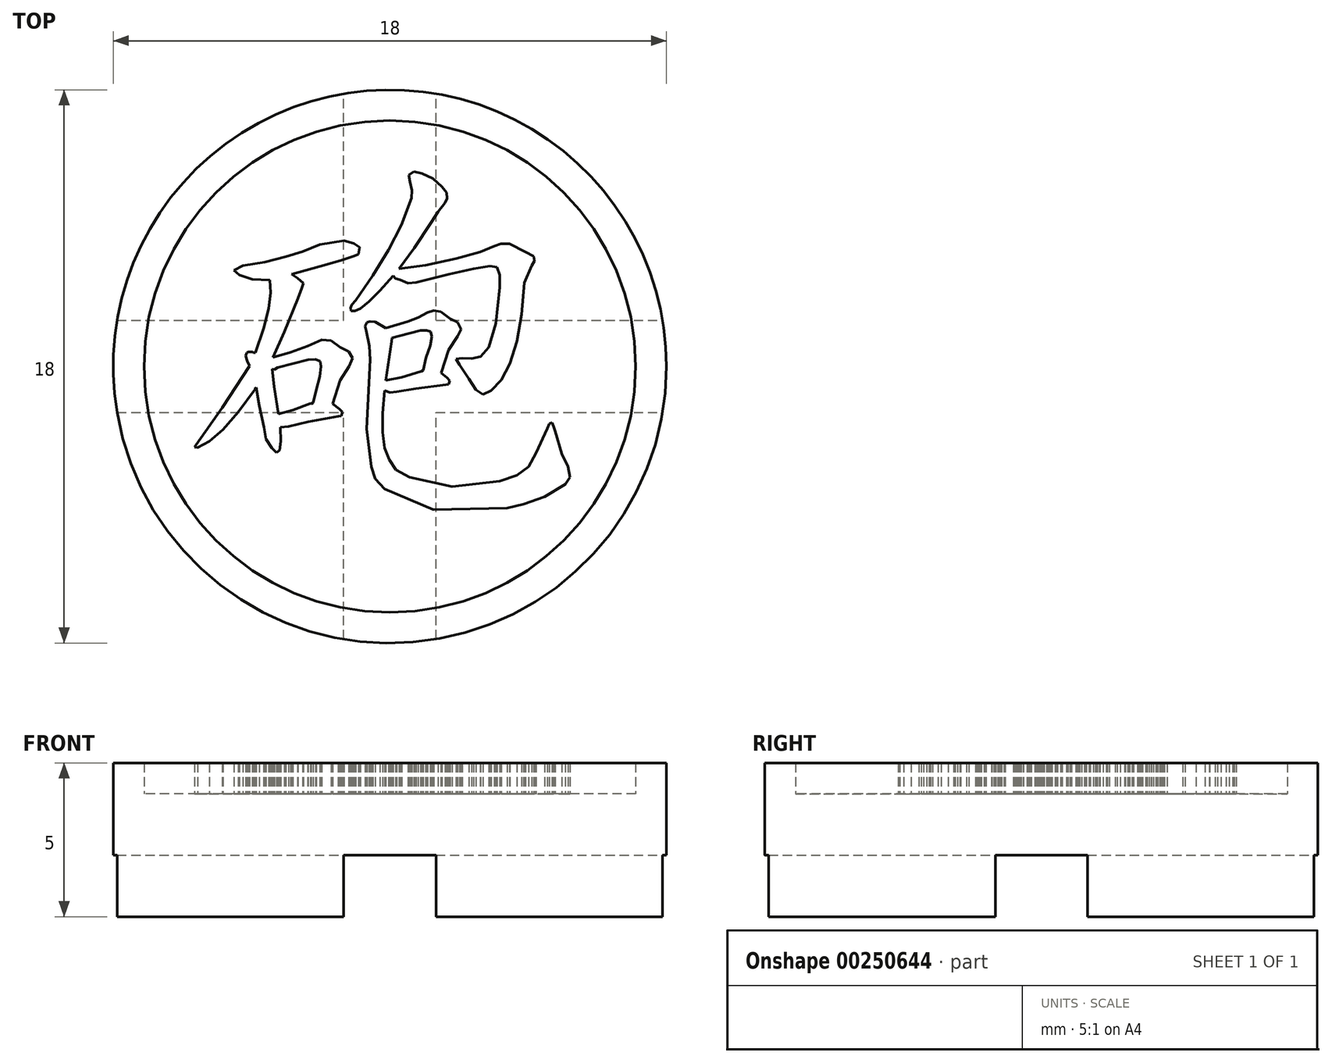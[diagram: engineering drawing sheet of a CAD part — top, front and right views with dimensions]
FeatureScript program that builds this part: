
annotation { "Feature Type Name" : "Feature", "Feature Type Description" : "" }
export const myFeature = defineFeature(function(context is Context, id is Id, definition is map)
    precondition{}
    {
        {
            var Q0;
            Q0=qCreatedBy(makeId("Top.planeOp"),FACE);
            var sketch = newSketch(context, id + "F0", { "sketchPlane" : qUnion([Q0])});
            skCircle(sketch, "E0", {"center": v(-31.33, 19.76) * mm, "radius": 9 * mm});
            skSolve(sketch);
        }
        {
            var Q0;
            Q0=qSketchRegion(id+"F0",true);
            extrude(context, id + "F1", {"entities" : qUnion([Q0]), "depth" : 4 * mm});
        }
        {
            var Q0;
            Q0=makeQuery(id+"F1.opExtrude","CAP_FACE",FACE,{"disambiguationData":[OSD([sQuery(id+"F0.wireOp",EDGE,"E0")])],"isStart":false});
            var sketch = newSketch(context, id + "F2", { "sketchPlane" : qUnion([Q0])});
            skCircle(sketch, "E1", {"center": v(-31.33, 19.76) * mm, "radius": 8 * mm});
            skCircle(sketch, "E2", {"center": v(-31.33, 19.76) * mm, "radius": 9 * mm});
            skSolve(sketch);
        }
        {
            var Q0;
            Q0=makeQuery(id+"F1.opExtrude","CAP_FACE",FACE,{"disambiguationData":[OSD([sQuery(id+"F0.wireOp",EDGE,"E0")])],"isStart":true});
            var sketch = newSketch(context, id + "F3", { "sketchPlane" : qUnion([Q0])});
            skLineSegment(sketch, "E3", {"start": v(-31.33, -19.76) * mm, "end": v(-22.33, -19.76) * mm, "construction": true});
            skLineSegment(sketch, "E4", {"start": v(-31.33, -19.76) * mm, "end": v(-31.33, -10.76) * mm, "construction": true});
            skLineSegment(sketch, "E5", {"start": v(-31.33, -19.76) * mm, "end": v(-40.33, -19.76) * mm, "construction": true});
            skLineSegment(sketch, "E6", {"start": v(-31.33, -19.76) * mm, "end": v(-31.33, -28.76) * mm, "construction": true});
            skLineSegment(sketch, "E7.bottom", {"start": v(-40.33, -28.76) * mm, "end": v(-22.33, -28.76) * mm});
            skLineSegment(sketch, "E7.top", {"start": v(-40.33, -10.76) * mm, "end": v(-22.33, -10.76) * mm});
            skLineSegment(sketch, "E7.left", {"start": v(-22.33, -10.76) * mm, "end": v(-22.33, -28.76) * mm});
            skLineSegment(sketch, "E7.right", {"start": v(-40.33, -10.76) * mm, "end": v(-40.33, -28.76) * mm});
            skPoint(sketch, "E8", {"position": v(-31.33, -28.76) * mm});
            skPoint(sketch, "E9", {"position": v(-40.33, -19.76) * mm});
            skPoint(sketch, "E10", {"position": v(-22.33, -19.76) * mm});
            skPoint(sketch, "E11", {"position": v(-31.33, -10.76) * mm});
            skLineSegment(sketch, "E12.bottom", {"start": v(-32.83, -10.76) * mm, "end": v(-29.83, -10.76) * mm});
            skLineSegment(sketch, "E12.top", {"start": v(-32.83, -28.76) * mm, "end": v(-29.83, -28.76) * mm});
            skLineSegment(sketch, "E12.left", {"start": v(-32.83, -10.76) * mm, "end": v(-32.83, -28.76) * mm});
            skLineSegment(sketch, "E12.right", {"start": v(-29.83, -10.76) * mm, "end": v(-29.83, -28.76) * mm});
            skLineSegment(sketch, "E13.bottom", {"start": v(-40.33, -18.26) * mm, "end": v(-22.33, -18.26) * mm});
            skLineSegment(sketch, "E13.top", {"start": v(-40.33, -21.26) * mm, "end": v(-22.33, -21.26) * mm});
            skLineSegment(sketch, "E13.left", {"start": v(-40.33, -18.26) * mm, "end": v(-40.33, -21.26) * mm});
            skLineSegment(sketch, "E13.right", {"start": v(-22.33, -18.26) * mm, "end": v(-22.33, -21.26) * mm});
            skSolve(sketch);
        }
        {
            var Q0;
            {var subQ1=sQuery(id+"F3.wireOp",EDGE,"E12.bottom");var subQ3=makeQuery(id+"F1.opExtrude","CAP_EDGE",EDGE,{"disambiguationData":[OSD([sQuery(id+"F0.wireOp",EDGE,"E0")])],"isStart":true});var subQ4=makeQuery(id+"F3.imprint","INTERSECT",VERTEX,{"derivedFrom":[subQ3,subQ1]});Q0=makeQuery(id+"F3.imprint","IMPRINT",FACE,{"disambiguationData":[TD([[makeQuery(id+"F3.imprint","IMPRINT",EDGE,{"disambiguationData":[TD([[subQ4,1.0]])],"derivedFrom":subQ3}),1.0]])]});}
            var Q1;
            {var subQ1=sQuery(id+"F3.wireOp",EDGE,"E12.bottom");var subQ3=makeQuery(id+"F1.opExtrude","CAP_EDGE",EDGE,{"disambiguationData":[OSD([sQuery(id+"F0.wireOp",EDGE,"E0")])],"isStart":true});var subQ4=makeQuery(id+"F3.imprint","INTERSECT",VERTEX,{"derivedFrom":[subQ3,subQ1]});Q1=makeQuery(id+"F3.imprint","IMPRINT",FACE,{"disambiguationData":[TD([[makeQuery(id+"F3.imprint","IMPRINT",EDGE,{"disambiguationData":[TD([[subQ4,-1.0]])],"derivedFrom":subQ3}),1.0]])]});}
            var Q2;
            {var subQ1=sQuery(id+"F3.wireOp",EDGE,"E12.top");var subQ3=makeQuery(id+"F1.opExtrude","CAP_EDGE",EDGE,{"disambiguationData":[OSD([sQuery(id+"F0.wireOp",EDGE,"E0")])],"isStart":true});var subQ4=makeQuery(id+"F3.imprint","INTERSECT",VERTEX,{"derivedFrom":[subQ3,subQ1]});Q2=makeQuery(id+"F3.imprint","IMPRINT",FACE,{"disambiguationData":[TD([[makeQuery(id+"F3.imprint","IMPRINT",EDGE,{"disambiguationData":[TD([[subQ4,-1.0]])],"derivedFrom":subQ3}),1.0]])]});}
            var Q3;
            {var subQ1=sQuery(id+"F3.wireOp",EDGE,"E12.top");var subQ3=makeQuery(id+"F1.opExtrude","CAP_EDGE",EDGE,{"disambiguationData":[OSD([sQuery(id+"F0.wireOp",EDGE,"E0")])],"isStart":true});var subQ4=makeQuery(id+"F3.imprint","INTERSECT",VERTEX,{"derivedFrom":[subQ3,subQ1]});Q3=makeQuery(id+"F3.imprint","IMPRINT",FACE,{"disambiguationData":[TD([[makeQuery(id+"F3.imprint","IMPRINT",EDGE,{"disambiguationData":[TD([[subQ4,1.0]])],"derivedFrom":subQ3}),1.0]])]});}
            var Q4;
            {var subQ0=sQuery(id+"F3.wireOp",EDGE,"E13.left");var subQ3=makeQuery(id+"F1.opExtrude","CAP_EDGE",EDGE,{"disambiguationData":[OSD([sQuery(id+"F0.wireOp",EDGE,"E0")])],"isStart":true});var subQ5=makeQuery(id+"F3.imprint","INTERSECT",VERTEX,{"derivedFrom":[subQ3,subQ0]});Q4=makeQuery(id+"F3.imprint","IMPRINT",FACE,{"disambiguationData":[TD([[makeQuery(id+"F3.imprint","IMPRINT",EDGE,{"disambiguationData":[TD([[subQ5,-1.0]])],"derivedFrom":subQ3}),1.0]])]});}
            var Q5;
            {var subQ0=sQuery(id+"F3.wireOp",EDGE,"E13.right");var subQ3=makeQuery(id+"F1.opExtrude","CAP_EDGE",EDGE,{"disambiguationData":[OSD([sQuery(id+"F0.wireOp",EDGE,"E0")])],"isStart":true});var subQ5=makeQuery(id+"F3.imprint","INTERSECT",VERTEX,{"derivedFrom":[subQ3,subQ0]});Q5=makeQuery(id+"F3.imprint","IMPRINT",FACE,{"disambiguationData":[TD([[makeQuery(id+"F3.imprint","IMPRINT",EDGE,{"disambiguationData":[TD([[subQ5,1.0]])],"derivedFrom":subQ3}),1.0]])]});}
            var Q6;
            {var subQ0=sQuery(id+"F3.wireOp",EDGE,"E13.left");var subQ3=makeQuery(id+"F1.opExtrude","CAP_EDGE",EDGE,{"disambiguationData":[OSD([sQuery(id+"F0.wireOp",EDGE,"E0")])],"isStart":true});var subQ5=makeQuery(id+"F3.imprint","INTERSECT",VERTEX,{"derivedFrom":[subQ3,subQ0]});Q6=makeQuery(id+"F3.imprint","IMPRINT",FACE,{"disambiguationData":[TD([[makeQuery(id+"F3.imprint","IMPRINT",EDGE,{"disambiguationData":[TD([[subQ5,1.0]])],"derivedFrom":subQ3}),1.0]])]});}
            var Q7;
            {var subQ0=sQuery(id+"F3.wireOp",EDGE,"E13.right");var subQ3=makeQuery(id+"F1.opExtrude","CAP_EDGE",EDGE,{"disambiguationData":[OSD([sQuery(id+"F0.wireOp",EDGE,"E0")])],"isStart":true});var subQ5=makeQuery(id+"F3.imprint","INTERSECT",VERTEX,{"derivedFrom":[subQ3,subQ0]});Q7=makeQuery(id+"F3.imprint","IMPRINT",FACE,{"disambiguationData":[TD([[makeQuery(id+"F3.imprint","IMPRINT",EDGE,{"disambiguationData":[TD([[subQ5,-1.0]])],"derivedFrom":subQ3}),1.0]])]});}
            var Q8;
            {var subQ3=makeQuery(id+"F1.opExtrude","CAP_EDGE",EDGE,{"disambiguationData":[OSD([sQuery(id+"F0.wireOp",EDGE,"E0")])],"isStart":true});var subQ5=sQuery(id+"F3.wireOp",EDGE,"E12.left");var subQ8=makeQuery(id+"F3.imprint","INTERSECT",VERTEX,{"disambiguationData":[OD(1.0)],"derivedFrom":[subQ3,subQ5]});Q8=makeQuery(id+"F3.imprint","IMPRINT",FACE,{"disambiguationData":[TD([[makeQuery(id+"F3.imprint","IMPRINT",EDGE,{"disambiguationData":[TD([[subQ8,-1.0]])],"derivedFrom":subQ3}),1.0]])]});}
            var Q9;
            {var subQ3=makeQuery(id+"F1.opExtrude","CAP_EDGE",EDGE,{"disambiguationData":[OSD([sQuery(id+"F0.wireOp",EDGE,"E0")])],"isStart":true});var subQ5=sQuery(id+"F3.wireOp",EDGE,"E12.right");var subQ8=makeQuery(id+"F3.imprint","INTERSECT",VERTEX,{"disambiguationData":[OD(1.0)],"derivedFrom":[subQ3,subQ5]});Q9=makeQuery(id+"F3.imprint","IMPRINT",FACE,{"disambiguationData":[TD([[makeQuery(id+"F3.imprint","IMPRINT",EDGE,{"disambiguationData":[TD([[subQ8,1.0]])],"derivedFrom":subQ3}),1.0]])]});}
            var Q10;
            {var subQ3=makeQuery(id+"F1.opExtrude","CAP_EDGE",EDGE,{"disambiguationData":[OSD([sQuery(id+"F0.wireOp",EDGE,"E0")])],"isStart":true});var subQ5=sQuery(id+"F3.wireOp",EDGE,"E12.left");var subQ8=makeQuery(id+"F3.imprint","INTERSECT",VERTEX,{"disambiguationData":[OD(0.0)],"derivedFrom":[subQ3,subQ5]});Q10=makeQuery(id+"F3.imprint","IMPRINT",FACE,{"disambiguationData":[TD([[makeQuery(id+"F3.imprint","IMPRINT",EDGE,{"disambiguationData":[TD([[subQ8,1.0]])],"derivedFrom":subQ3}),1.0]])]});}
            var Q11;
            {var subQ3=makeQuery(id+"F1.opExtrude","CAP_EDGE",EDGE,{"disambiguationData":[OSD([sQuery(id+"F0.wireOp",EDGE,"E0")])],"isStart":true});var subQ5=sQuery(id+"F3.wireOp",EDGE,"E12.right");var subQ8=makeQuery(id+"F3.imprint","INTERSECT",VERTEX,{"disambiguationData":[OD(0.0)],"derivedFrom":[subQ3,subQ5]});Q11=makeQuery(id+"F3.imprint","IMPRINT",FACE,{"disambiguationData":[TD([[makeQuery(id+"F3.imprint","IMPRINT",EDGE,{"disambiguationData":[TD([[subQ8,-1.0]])],"derivedFrom":subQ3}),1.0]])]});}
            var Q12;
            {var subQ2=sQuery(id+"F3.wireOp",EDGE,"E12.left");var subQ4=sQuery(id+"F3.wireOp",EDGE,"E13.bottom");var subQ8=makeQuery(id+"F3.imprint","INTERSECT",VERTEX,{"derivedFrom":[subQ2,subQ4]});Q12=makeQuery(id+"F3.imprint","IMPRINT",FACE,{"disambiguationData":[TD([[makeQuery(id+"F3.imprint","IMPRINT",EDGE,{"disambiguationData":[TD([[subQ8,1.0]])],"derivedFrom":subQ2}),1.0]])]});}
            var Q13;
            {var subQ1=sQuery(id+"F3.wireOp",EDGE,"E12.left");var subQ5=sQuery(id+"F3.wireOp",EDGE,"E13.bottom");var subQ6=makeQuery(id+"F3.imprint","INTERSECT",VERTEX,{"derivedFrom":[subQ1,subQ5]});Q13=makeQuery(id+"F3.imprint","IMPRINT",FACE,{"disambiguationData":[TD([[makeQuery(id+"F3.imprint","IMPRINT",EDGE,{"disambiguationData":[TD([[subQ6,-1.0]])],"derivedFrom":subQ1}),-1.0]])]});}
            var Q14;
            {var subQ0=sQuery(id+"F3.wireOp",EDGE,"E13.top");var subQ1=sQuery(id+"F3.wireOp",EDGE,"E12.left");var subQ2=makeQuery(id+"F3.imprint","INTERSECT",VERTEX,{"derivedFrom":[subQ1,subQ0]});Q14=makeQuery(id+"F3.imprint","IMPRINT",FACE,{"disambiguationData":[TD([[makeQuery(id+"F3.imprint","IMPRINT",EDGE,{"disambiguationData":[TD([[subQ2,-1.0]])],"derivedFrom":subQ1}),1.0]])]});}
            var Q15;
            {var subQ2=sQuery(id+"F3.wireOp",EDGE,"E13.bottom");var subQ5=sQuery(id+"F3.wireOp",EDGE,"E12.right");var subQ8=makeQuery(id+"F3.imprint","INTERSECT",VERTEX,{"derivedFrom":[subQ5,subQ2]});Q15=makeQuery(id+"F3.imprint","IMPRINT",FACE,{"disambiguationData":[TD([[makeQuery(id+"F3.imprint","IMPRINT",EDGE,{"disambiguationData":[TD([[subQ8,-1.0]])],"derivedFrom":subQ5}),1.0]])]});}
            var Q16;
            {var subQ0=sQuery(id+"F3.wireOp",EDGE,"E13.bottom");var subQ1=sQuery(id+"F3.wireOp",EDGE,"E12.left");var subQ2=makeQuery(id+"F3.imprint","INTERSECT",VERTEX,{"derivedFrom":[subQ1,subQ0]});Q16=makeQuery(id+"F3.imprint","IMPRINT",FACE,{"disambiguationData":[TD([[makeQuery(id+"F3.imprint","IMPRINT",EDGE,{"disambiguationData":[TD([[subQ2,-1.0]])],"derivedFrom":subQ1}),1.0]])]});}
            extrude(context, id + "F4", {"entities" : qUnion([Q0, Q1, Q2, Q3, Q4, Q5, Q6, Q7, Q8, Q9, Q10, Q11, Q12, Q13, Q14, Q15, Q16]), "operationType" : NewBodyOperationType.REMOVE, "oppositeDirection" : true, "depth" : 2 * mm});
        }
        {
            var Q0;
            Q0=qSketchRegion(id+"F2",true);
            var Q1;
            Q1=makeQuery(id+"F2.imprint","IMPRINT",FACE,{"disambiguationData":[TD([[makeQuery(id+"F2.imprint","IMPRINT",EDGE,{"derivedFrom":sQuery(id+"F2.wireOp",EDGE,"hKqnuJLd-dfdz-vJIs-yDKo-c4hLNRw30SuP")}),-1.0]])]});
            extrude(context, id + "F5", {"entities" : qUnion([Q0, Q1]), "operationType" : NewBodyOperationType.ADD, "depth" : 1 * mm});
        }
        {
            var Q0;
            Q0=makeQuery(id+"F1.opExtrude","CAP_FACE",FACE,{"disambiguationData":[OSD([sQuery(id+"F0.wireOp",EDGE,"E0")])],"isStart":false});
            var sketch = newSketch(context, id + "F6", { "sketchPlane" : qUnion([Q0])});
            skLineSegment(sketch, "E14", {"start": v(-34.89, 17.78) * mm, "end": v(-34.63, 17.8) * mm});
            skLineSegment(sketch, "E15", {"start": v(-34.63, 17.8) * mm, "end": v(-33.99, 17.96) * mm});
            skLineSegment(sketch, "E16", {"start": v(-33.99, 17.96) * mm, "end": v(-33.01, 18.13) * mm});
            skLineSegment(sketch, "E17", {"start": v(-33.01, 18.13) * mm, "end": v(-32.92, 18.15) * mm});
            skLineSegment(sketch, "E18", {"start": v(-32.92, 18.15) * mm, "end": v(-32.87, 18.28) * mm});
            skLineSegment(sketch, "E19", {"start": v(-32.87, 18.28) * mm, "end": v(-32.97, 18.38) * mm});
            skLineSegment(sketch, "E20", {"start": v(-32.97, 18.38) * mm, "end": v(-33.2, 18.54) * mm});
            skLineSegment(sketch, "E21", {"start": v(-33.2, 18.54) * mm, "end": v(-32.95, 19.3) * mm});
            skLineSegment(sketch, "E22", {"start": v(-32.95, 19.3) * mm, "end": v(-32.66, 19.76) * mm});
            skLineSegment(sketch, "E23", {"start": v(-32.66, 19.76) * mm, "end": v(-32.55, 20.03) * mm});
            skLineSegment(sketch, "E24", {"start": v(-32.55, 20.03) * mm, "end": v(-32.67, 20.25) * mm});
            skLineSegment(sketch, "E25", {"start": v(-32.67, 20.25) * mm, "end": v(-32.95, 20.39) * mm});
            skLineSegment(sketch, "E26", {"start": v(-32.95, 20.39) * mm, "end": v(-33.24, 20.6) * mm});
            skLineSegment(sketch, "E27", {"start": v(-33.24, 20.6) * mm, "end": v(-33.55, 20.63) * mm});
            skLineSegment(sketch, "E28", {"start": v(-33.55, 20.63) * mm, "end": v(-34, 20.42) * mm});
            skLineSegment(sketch, "E29", {"start": v(-34, 20.42) * mm, "end": v(-34.56, 20.22) * mm});
            skLineSegment(sketch, "E30", {"start": v(-34.56, 20.22) * mm, "end": v(-35.14, 20.05) * mm});
            skLineSegment(sketch, "E31", {"start": v(-35.14, 20.05) * mm, "end": v(-34.77, 20.89) * mm});
            skLineSegment(sketch, "E32", {"start": v(-34.77, 20.89) * mm, "end": v(-34.32, 21.97) * mm});
            skLineSegment(sketch, "E33", {"start": v(-34.32, 21.97) * mm, "end": v(-34.2, 22.31) * mm});
            skLineSegment(sketch, "E34", {"start": v(-34.2, 22.31) * mm, "end": v(-34.14, 22.47) * mm});
            skLineSegment(sketch, "E35", {"start": v(-34.14, 22.47) * mm, "end": v(-34.33, 22.63) * mm});
            skLineSegment(sketch, "E36", {"start": v(-34.33, 22.63) * mm, "end": v(-34.52, 22.75) * mm});
            skLineSegment(sketch, "E37", {"start": v(-34.52, 22.75) * mm, "end": v(-33.6, 23.01) * mm});
            skLineSegment(sketch, "E38", {"start": v(-33.6, 23.01) * mm, "end": v(-32.94, 23.2) * mm});
            skLineSegment(sketch, "E39", {"start": v(-32.94, 23.2) * mm, "end": v(-32.52, 23.34) * mm});
            skLineSegment(sketch, "E40", {"start": v(-32.52, 23.34) * mm, "end": v(-32.36, 23.4) * mm});
            skLineSegment(sketch, "E41", {"start": v(-32.36, 23.4) * mm, "end": v(-32.32, 23.63) * mm});
            skLineSegment(sketch, "E42", {"start": v(-32.32, 23.63) * mm, "end": v(-32.5, 23.76) * mm});
            skLineSegment(sketch, "E43", {"start": v(-32.5, 23.76) * mm, "end": v(-32.82, 23.85) * mm});
            skLineSegment(sketch, "E44", {"start": v(-32.82, 23.85) * mm, "end": v(-33.62, 23.72) * mm});
            skLineSegment(sketch, "E45", {"start": v(-33.62, 23.72) * mm, "end": v(-34.17, 23.5) * mm});
            skLineSegment(sketch, "E46", {"start": v(-34.17, 23.5) * mm, "end": v(-34.72, 23.33) * mm});
            skLineSegment(sketch, "E47", {"start": v(-34.72, 23.33) * mm, "end": v(-35.4, 23.15) * mm});
            skLineSegment(sketch, "E48", {"start": v(-35.4, 23.15) * mm, "end": v(-36.1, 23.04) * mm});
            skLineSegment(sketch, "E49", {"start": v(-36.1, 23.04) * mm, "end": v(-36.4, 22.9) * mm});
            skLineSegment(sketch, "E50", {"start": v(-36.4, 22.9) * mm, "end": v(-36.23, 22.73) * mm});
            skLineSegment(sketch, "E51", {"start": v(-36.23, 22.73) * mm, "end": v(-35.81, 22.59) * mm});
            skLineSegment(sketch, "E52", {"start": v(-35.81, 22.59) * mm, "end": v(-35.23, 22.57) * mm});
            skLineSegment(sketch, "E53", {"start": v(-35.23, 22.57) * mm, "end": v(-35.22, 22.16) * mm});
            skLineSegment(sketch, "E54", {"start": v(-35.22, 22.16) * mm, "end": v(-35.28, 21.64) * mm});
            skLineSegment(sketch, "E55", {"start": v(-35.28, 21.64) * mm, "end": v(-35.43, 20.99) * mm});
            skLineSegment(sketch, "E56", {"start": v(-35.43, 20.99) * mm, "end": v(-35.7, 20.2) * mm});
            skLineSegment(sketch, "E57", {"start": v(-35.7, 20.2) * mm, "end": v(-35.77, 20.21) * mm});
            skLineSegment(sketch, "E58", {"start": v(-35.77, 20.21) * mm, "end": v(-35.8, 20.23) * mm});
            skLineSegment(sketch, "E59", {"start": v(-35.8, 20.23) * mm, "end": v(-35.93, 20.23) * mm});
            skLineSegment(sketch, "E60", {"start": v(-35.93, 20.23) * mm, "end": v(-35.98, 20.2) * mm});
            skLineSegment(sketch, "E61", {"start": v(-35.98, 20.2) * mm, "end": v(-36.03, 20.1) * mm});
            skLineSegment(sketch, "E62", {"start": v(-36.03, 20.1) * mm, "end": v(-35.97, 19.95) * mm});
            skLineSegment(sketch, "E63", {"start": v(-35.97, 19.95) * mm, "end": v(-35.9, 19.78) * mm});
            skLineSegment(sketch, "E64", {"start": v(-35.9, 19.78) * mm, "end": v(-36.79, 18.41) * mm});
            skLineSegment(sketch, "E65", {"start": v(-36.79, 18.41) * mm, "end": v(-37.63, 17.22) * mm});
            skLineSegment(sketch, "E66", {"start": v(-37.63, 17.22) * mm, "end": v(-37.69, 17.14) * mm});
            skLineSegment(sketch, "E67", {"start": v(-37.69, 17.14) * mm, "end": v(-37.58, 17.12) * mm});
            skLineSegment(sketch, "E68", {"start": v(-37.58, 17.12) * mm, "end": v(-37.2, 17.32) * mm});
            skLineSegment(sketch, "E69", {"start": v(-37.2, 17.32) * mm, "end": v(-36.76, 17.7) * mm});
            skLineSegment(sketch, "E70", {"start": v(-36.76, 17.7) * mm, "end": v(-36.27, 18.27) * mm});
            skLineSegment(sketch, "E71", {"start": v(-36.27, 18.27) * mm, "end": v(-35.72, 19.01) * mm});
            skLineSegment(sketch, "E72", {"start": v(-35.72, 19.01) * mm, "end": v(-35.73, 19.03) * mm});
            skLineSegment(sketch, "E73", {"start": v(-35.73, 19.03) * mm, "end": v(-35.68, 19.08) * mm});
            skLineSegment(sketch, "E74", {"start": v(-35.68, 19.08) * mm, "end": v(-35.57, 18.47) * mm});
            skLineSegment(sketch, "E75", {"start": v(-35.57, 18.47) * mm, "end": v(-35.43, 17.78) * mm});
            skLineSegment(sketch, "E76", {"start": v(-35.43, 17.78) * mm, "end": v(-35.36, 17.4) * mm});
            skLineSegment(sketch, "E77", {"start": v(-35.36, 17.4) * mm, "end": v(-35.18, 17.11) * mm});
            skLineSegment(sketch, "E78", {"start": v(-35.18, 17.11) * mm, "end": v(-35.02, 16.95) * mm});
            skLineSegment(sketch, "E79", {"start": v(-35.02, 16.95) * mm, "end": v(-34.92, 17.03) * mm});
            skLineSegment(sketch, "E80", {"start": v(-34.92, 17.03) * mm, "end": v(-34.88, 17.32) * mm});
            skLineSegment(sketch, "E81", {"start": v(-34.88, 17.32) * mm, "end": v(-34.89, 17.78) * mm});
            skLineSegment(sketch, "E82", {"start": v(-33.92, 18.55) * mm, "end": v(-34.49, 18.34) * mm});
            skLineSegment(sketch, "E83", {"start": v(-34.49, 18.34) * mm, "end": v(-34.95, 18.21) * mm});
            skLineSegment(sketch, "E84", {"start": v(-34.95, 18.21) * mm, "end": v(-35.1, 19.1) * mm});
            skLineSegment(sketch, "E85", {"start": v(-35.1, 19.1) * mm, "end": v(-35.16, 19.67) * mm});
            skLineSegment(sketch, "E86", {"start": v(-35.16, 19.67) * mm, "end": v(-35.09, 19.67) * mm});
            skLineSegment(sketch, "E87", {"start": v(-35.09, 19.67) * mm, "end": v(-34.98, 19.72) * mm});
            skLineSegment(sketch, "E88", {"start": v(-34.98, 19.72) * mm, "end": v(-33.99, 19.97) * mm});
            skLineSegment(sketch, "E89", {"start": v(-33.99, 19.97) * mm, "end": v(-33.75, 20) * mm});
            skLineSegment(sketch, "E90", {"start": v(-33.75, 20) * mm, "end": v(-33.6, 19.93) * mm});
            skLineSegment(sketch, "E91", {"start": v(-33.6, 19.93) * mm, "end": v(-33.57, 19.76) * mm});
            skLineSegment(sketch, "E92", {"start": v(-33.57, 19.76) * mm, "end": v(-33.62, 19.43) * mm});
            skLineSegment(sketch, "E93", {"start": v(-33.62, 19.43) * mm, "end": v(-33.73, 19) * mm});
            skLineSegment(sketch, "E94", {"start": v(-33.73, 19) * mm, "end": v(-33.83, 18.58) * mm});
            skLineSegment(sketch, "E95", {"start": v(-33.83, 18.58) * mm, "end": v(-33.89, 18.55) * mm});
            skLineSegment(sketch, "E96", {"start": v(-33.89, 18.55) * mm, "end": v(-33.92, 18.55) * mm});
            skLineSegment(sketch, "E97", {"start": v(-31.23, 22.7) * mm, "end": v(-31.14, 22.62) * mm});
            skLineSegment(sketch, "E98", {"start": v(-31.14, 22.62) * mm, "end": v(-31, 22.58) * mm});
            skLineSegment(sketch, "E99", {"start": v(-31, 22.58) * mm, "end": v(-30.74, 22.47) * mm});
            skLineSegment(sketch, "E100", {"start": v(-30.74, 22.47) * mm, "end": v(-30.48, 22.5) * mm});
            skLineSegment(sketch, "E101", {"start": v(-30.48, 22.5) * mm, "end": v(-29.41, 22.76) * mm});
            skLineSegment(sketch, "E102", {"start": v(-29.41, 22.76) * mm, "end": v(-28.6, 22.94) * mm});
            skLineSegment(sketch, "E103", {"start": v(-28.6, 22.94) * mm, "end": v(-28.08, 23.03) * mm});
            skLineSegment(sketch, "E104", {"start": v(-28.08, 23.03) * mm, "end": v(-27.84, 23) * mm});
            skLineSegment(sketch, "E105", {"start": v(-27.84, 23) * mm, "end": v(-27.76, 22.73) * mm});
            skLineSegment(sketch, "E106", {"start": v(-27.76, 22.73) * mm, "end": v(-27.75, 22.32) * mm});
            skLineSegment(sketch, "E107", {"start": v(-27.75, 22.32) * mm, "end": v(-27.88, 21.16) * mm});
            skLineSegment(sketch, "E108", {"start": v(-27.88, 21.16) * mm, "end": v(-28.1, 20.38) * mm});
            skLineSegment(sketch, "E109", {"start": v(-28.1, 20.38) * mm, "end": v(-28.38, 20.08) * mm});
            skLineSegment(sketch, "E110", {"start": v(-28.38, 20.08) * mm, "end": v(-28.67, 20.01) * mm});
            skLineSegment(sketch, "E111", {"start": v(-28.67, 20.01) * mm, "end": v(-28.97, 20.02) * mm});
            skLineSegment(sketch, "E112", {"start": v(-28.97, 20.02) * mm, "end": v(-29.18, 20) * mm});
            skLineSegment(sketch, "E113", {"start": v(-29.18, 20) * mm, "end": v(-29.06, 19.81) * mm});
            skLineSegment(sketch, "E114", {"start": v(-29.06, 19.81) * mm, "end": v(-28.76, 19.36) * mm});
            skLineSegment(sketch, "E115", {"start": v(-28.76, 19.36) * mm, "end": v(-28.53, 19) * mm});
            skLineSegment(sketch, "E116", {"start": v(-28.53, 19) * mm, "end": v(-28.3, 18.85) * mm});
            skLineSegment(sketch, "E117", {"start": v(-28.3, 18.85) * mm, "end": v(-28.04, 18.97) * mm});
            skLineSegment(sketch, "E118", {"start": v(-28.04, 18.97) * mm, "end": v(-27.7, 19.31) * mm});
            skLineSegment(sketch, "E119", {"start": v(-27.7, 19.31) * mm, "end": v(-27.42, 19.85) * mm});
            skLineSegment(sketch, "E120", {"start": v(-27.42, 19.85) * mm, "end": v(-27.2, 20.57) * mm});
            skLineSegment(sketch, "E121", {"start": v(-27.2, 20.57) * mm, "end": v(-27.04, 21.46) * mm});
            skLineSegment(sketch, "E122", {"start": v(-27.04, 21.46) * mm, "end": v(-26.95, 22.48) * mm});
            skLineSegment(sketch, "E123", {"start": v(-26.95, 22.48) * mm, "end": v(-26.72, 23.04) * mm});
            skLineSegment(sketch, "E124", {"start": v(-26.72, 23.04) * mm, "end": v(-26.63, 23.19) * mm});
            skLineSegment(sketch, "E125", {"start": v(-26.63, 23.19) * mm, "end": v(-26.65, 23.34) * mm});
            skLineSegment(sketch, "E126", {"start": v(-26.65, 23.34) * mm, "end": v(-26.92, 23.49) * mm});
            skLineSegment(sketch, "E127", {"start": v(-26.92, 23.49) * mm, "end": v(-27.44, 23.75) * mm});
            skLineSegment(sketch, "E128", {"start": v(-27.44, 23.75) * mm, "end": v(-27.71, 23.76) * mm});
            skLineSegment(sketch, "E129", {"start": v(-27.71, 23.76) * mm, "end": v(-27.94, 23.67) * mm});
            skLineSegment(sketch, "E130", {"start": v(-27.94, 23.67) * mm, "end": v(-28.39, 23.48) * mm});
            skLineSegment(sketch, "E131", {"start": v(-28.39, 23.48) * mm, "end": v(-29.18, 23.26) * mm});
            skLineSegment(sketch, "E132", {"start": v(-29.18, 23.26) * mm, "end": v(-30.17, 23.05) * mm});
            skLineSegment(sketch, "E133", {"start": v(-30.17, 23.05) * mm, "end": v(-31.03, 22.94) * mm});
            skLineSegment(sketch, "E134", {"start": v(-31.03, 22.94) * mm, "end": v(-30.53, 23.61) * mm});
            skLineSegment(sketch, "E135", {"start": v(-30.53, 23.61) * mm, "end": v(-29.98, 24.43) * mm});
            skLineSegment(sketch, "E136", {"start": v(-29.98, 24.43) * mm, "end": v(-29.76, 24.8) * mm});
            skLineSegment(sketch, "E137", {"start": v(-29.76, 24.8) * mm, "end": v(-29.54, 25.09) * mm});
            skLineSegment(sketch, "E138", {"start": v(-29.54, 25.09) * mm, "end": v(-29.46, 25.22) * mm});
            skLineSegment(sketch, "E139", {"start": v(-29.46, 25.22) * mm, "end": v(-29.48, 25.42) * mm});
            skLineSegment(sketch, "E140", {"start": v(-29.48, 25.42) * mm, "end": v(-29.63, 25.6) * mm});
            skLineSegment(sketch, "E141", {"start": v(-29.63, 25.6) * mm, "end": v(-29.93, 25.88) * mm});
            skLineSegment(sketch, "E142", {"start": v(-29.93, 25.88) * mm, "end": v(-30.28, 26.03) * mm});
            skLineSegment(sketch, "E143", {"start": v(-30.28, 26.03) * mm, "end": v(-30.54, 26.1) * mm});
            skLineSegment(sketch, "E144", {"start": v(-30.54, 26.1) * mm, "end": v(-30.72, 25.98) * mm});
            skLineSegment(sketch, "E145", {"start": v(-30.72, 25.98) * mm, "end": v(-30.68, 25.77) * mm});
            skLineSegment(sketch, "E146", {"start": v(-30.68, 25.77) * mm, "end": v(-30.61, 25.49) * mm});
            skLineSegment(sketch, "E147", {"start": v(-30.61, 25.49) * mm, "end": v(-30.62, 25.23) * mm});
            skLineSegment(sketch, "E148", {"start": v(-30.62, 25.23) * mm, "end": v(-30.96, 24.36) * mm});
            skLineSegment(sketch, "E149", {"start": v(-30.96, 24.36) * mm, "end": v(-31.37, 23.55) * mm});
            skLineSegment(sketch, "E150", {"start": v(-31.37, 23.55) * mm, "end": v(-31.88, 22.72) * mm});
            skLineSegment(sketch, "E151", {"start": v(-31.88, 22.72) * mm, "end": v(-32.45, 21.9) * mm});
            skLineSegment(sketch, "E152", {"start": v(-32.45, 21.9) * mm, "end": v(-32.57, 21.77) * mm});
            skLineSegment(sketch, "E153", {"start": v(-32.57, 21.77) * mm, "end": v(-32.6, 21.67) * mm});
            skLineSegment(sketch, "E154", {"start": v(-32.6, 21.67) * mm, "end": v(-32.59, 21.57) * mm});
            skLineSegment(sketch, "E155", {"start": v(-32.59, 21.57) * mm, "end": v(-32.46, 21.56) * mm});
            skLineSegment(sketch, "E156", {"start": v(-32.46, 21.56) * mm, "end": v(-32.28, 21.64) * mm});
            skLineSegment(sketch, "E157", {"start": v(-32.28, 21.64) * mm, "end": v(-32, 21.87) * mm});
            skLineSegment(sketch, "E158", {"start": v(-32, 21.87) * mm, "end": v(-31.65, 22.23) * mm});
            skLineSegment(sketch, "E159", {"start": v(-31.65, 22.23) * mm, "end": v(-31.23, 22.7) * mm});
            skLineSegment(sketch, "E160", {"start": v(-31.46, 21) * mm, "end": v(-31.8, 21.2) * mm});
            skLineSegment(sketch, "E161", {"start": v(-31.8, 21.2) * mm, "end": v(-31.98, 21.23) * mm});
            skLineSegment(sketch, "E162", {"start": v(-31.98, 21.23) * mm, "end": v(-32.07, 21.2) * mm});
            skLineSegment(sketch, "E163", {"start": v(-32.07, 21.2) * mm, "end": v(-32.13, 21.07) * mm});
            skLineSegment(sketch, "E164", {"start": v(-32.13, 21.07) * mm, "end": v(-32.1, 20.92) * mm});
            skLineSegment(sketch, "E165", {"start": v(-32.1, 20.92) * mm, "end": v(-32, 20.42) * mm});
            skLineSegment(sketch, "E166", {"start": v(-32, 20.42) * mm, "end": v(-31.98, 19.97) * mm});
            skLineSegment(sketch, "E167", {"start": v(-31.98, 19.97) * mm, "end": v(-32.1, 17.74) * mm});
            skLineSegment(sketch, "E168", {"start": v(-32.1, 17.74) * mm, "end": v(-31.94, 16.5) * mm});
            skLineSegment(sketch, "E169", {"start": v(-31.94, 16.5) * mm, "end": v(-31.8, 16.1) * mm});
            skLineSegment(sketch, "E170", {"start": v(-31.8, 16.1) * mm, "end": v(-31.5, 15.77) * mm});
            skLineSegment(sketch, "E171", {"start": v(-31.5, 15.77) * mm, "end": v(-29.92, 15.1) * mm});
            skLineSegment(sketch, "E172", {"start": v(-29.92, 15.1) * mm, "end": v(-27.52, 15.16) * mm});
            skLineSegment(sketch, "E173", {"start": v(-27.52, 15.16) * mm, "end": v(-26.98, 15.27) * mm});
            skLineSegment(sketch, "E174", {"start": v(-26.98, 15.27) * mm, "end": v(-26.3, 15.52) * mm});
            skLineSegment(sketch, "E175", {"start": v(-26.3, 15.52) * mm, "end": v(-25.63, 15.93) * mm});
            skLineSegment(sketch, "E176", {"start": v(-25.63, 15.93) * mm, "end": v(-25.47, 16.16) * mm});
            skLineSegment(sketch, "E177", {"start": v(-25.47, 16.16) * mm, "end": v(-25.53, 16.5) * mm});
            skLineSegment(sketch, "E178", {"start": v(-25.53, 16.5) * mm, "end": v(-25.74, 16.91) * mm});
            skLineSegment(sketch, "E179", {"start": v(-25.74, 16.91) * mm, "end": v(-25.95, 17.65) * mm});
            skLineSegment(sketch, "E180", {"start": v(-25.95, 17.65) * mm, "end": v(-26, 17.8) * mm});
            skLineSegment(sketch, "E181", {"start": v(-26, 17.8) * mm, "end": v(-26.06, 17.94) * mm});
            skLineSegment(sketch, "E182", {"start": v(-26.06, 17.94) * mm, "end": v(-26.14, 17.89) * mm});
            skLineSegment(sketch, "E183", {"start": v(-26.14, 17.89) * mm, "end": v(-26.2, 17.74) * mm});
            skLineSegment(sketch, "E184", {"start": v(-26.2, 17.74) * mm, "end": v(-26.57, 16.95) * mm});
            skLineSegment(sketch, "E185", {"start": v(-26.57, 16.95) * mm, "end": v(-26.82, 16.5) * mm});
            skLineSegment(sketch, "E186", {"start": v(-26.82, 16.5) * mm, "end": v(-27.2, 16.22) * mm});
            skLineSegment(sketch, "E187", {"start": v(-27.2, 16.22) * mm, "end": v(-27.75, 16.02) * mm});
            skLineSegment(sketch, "E188", {"start": v(-27.75, 16.02) * mm, "end": v(-29.3, 15.85) * mm});
            skLineSegment(sketch, "E189", {"start": v(-29.3, 15.85) * mm, "end": v(-30.69, 16.15) * mm});
            skLineSegment(sketch, "E190", {"start": v(-30.69, 16.15) * mm, "end": v(-31.14, 16.4) * mm});
            skLineSegment(sketch, "E191", {"start": v(-31.14, 16.4) * mm, "end": v(-31.35, 16.73) * mm});
            skLineSegment(sketch, "E192", {"start": v(-31.35, 16.73) * mm, "end": v(-31.5, 17.1) * mm});
            skLineSegment(sketch, "E193", {"start": v(-31.5, 17.1) * mm, "end": v(-31.57, 17.62) * mm});
            skLineSegment(sketch, "E194", {"start": v(-31.57, 17.62) * mm, "end": v(-31.56, 18.24) * mm});
            skLineSegment(sketch, "E195", {"start": v(-31.56, 18.24) * mm, "end": v(-31.5, 18.97) * mm});
            skLineSegment(sketch, "E196", {"start": v(-31.5, 18.97) * mm, "end": v(-31.32, 18.9) * mm});
            skLineSegment(sketch, "E197", {"start": v(-31.32, 18.9) * mm, "end": v(-31.1, 18.94) * mm});
            skLineSegment(sketch, "E198", {"start": v(-31.1, 18.94) * mm, "end": v(-30.48, 19.04) * mm});
            skLineSegment(sketch, "E199", {"start": v(-30.48, 19.04) * mm, "end": v(-29.51, 19.16) * mm});
            skLineSegment(sketch, "E200", {"start": v(-29.51, 19.16) * mm, "end": v(-29.42, 19.18) * mm});
            skLineSegment(sketch, "E201", {"start": v(-29.42, 19.18) * mm, "end": v(-29.38, 19.29) * mm});
            skLineSegment(sketch, "E202", {"start": v(-29.38, 19.29) * mm, "end": v(-29.47, 19.4) * mm});
            skLineSegment(sketch, "E203", {"start": v(-29.47, 19.4) * mm, "end": v(-29.66, 19.55) * mm});
            skLineSegment(sketch, "E204", {"start": v(-29.66, 19.55) * mm, "end": v(-29.42, 20.29) * mm});
            skLineSegment(sketch, "E205", {"start": v(-29.42, 20.29) * mm, "end": v(-29.13, 20.73) * mm});
            skLineSegment(sketch, "E206", {"start": v(-29.13, 20.73) * mm, "end": v(-29, 20.97) * mm});
            skLineSegment(sketch, "E207", {"start": v(-29, 20.97) * mm, "end": v(-29.13, 21.2) * mm});
            skLineSegment(sketch, "E208", {"start": v(-29.13, 21.2) * mm, "end": v(-29.37, 21.32) * mm});
            skLineSegment(sketch, "E209", {"start": v(-29.37, 21.32) * mm, "end": v(-29.67, 21.53) * mm});
            skLineSegment(sketch, "E210", {"start": v(-29.67, 21.53) * mm, "end": v(-29.9, 21.58) * mm});
            skLineSegment(sketch, "E211", {"start": v(-29.9, 21.58) * mm, "end": v(-30.1, 21.52) * mm});
            skLineSegment(sketch, "E212", {"start": v(-30.1, 21.52) * mm, "end": v(-30.41, 21.35) * mm});
            skLineSegment(sketch, "E213", {"start": v(-30.41, 21.35) * mm, "end": v(-30.74, 21.22) * mm});
            skLineSegment(sketch, "E214", {"start": v(-30.74, 21.22) * mm, "end": v(-31.46, 21) * mm});
            skLineSegment(sketch, "E215", {"start": v(-31.28, 20.58) * mm, "end": v(-31.27, 20.7) * mm});
            skLineSegment(sketch, "E216", {"start": v(-31.27, 20.7) * mm, "end": v(-31.02, 20.76) * mm});
            skLineSegment(sketch, "E217", {"start": v(-31.02, 20.76) * mm, "end": v(-30.33, 20.93) * mm});
            skLineSegment(sketch, "E218", {"start": v(-30.33, 20.93) * mm, "end": v(-30.13, 20.93) * mm});
            skLineSegment(sketch, "E219", {"start": v(-30.13, 20.93) * mm, "end": v(-30, 20.9) * mm});
            skLineSegment(sketch, "E220", {"start": v(-30, 20.9) * mm, "end": v(-29.97, 20.72) * mm});
            skLineSegment(sketch, "E221", {"start": v(-29.97, 20.72) * mm, "end": v(-30.02, 20.43) * mm});
            skLineSegment(sketch, "E222", {"start": v(-30.02, 20.43) * mm, "end": v(-30.15, 20.04) * mm});
            skLineSegment(sketch, "E223", {"start": v(-30.15, 20.04) * mm, "end": v(-30.25, 19.63) * mm});
            skLineSegment(sketch, "E224", {"start": v(-30.25, 19.63) * mm, "end": v(-30.31, 19.6) * mm});
            skLineSegment(sketch, "E225", {"start": v(-30.31, 19.6) * mm, "end": v(-30.32, 19.6) * mm});
            skLineSegment(sketch, "E226", {"start": v(-30.32, 19.6) * mm, "end": v(-30.95, 19.41) * mm});
            skLineSegment(sketch, "E227", {"start": v(-30.95, 19.41) * mm, "end": v(-31.46, 19.3) * mm});
            skLineSegment(sketch, "E228", {"start": v(-31.46, 19.3) * mm, "end": v(-31.28, 20.58) * mm});
            skSolve(sketch);
        }
        {
            var Q0;
            Q0 = qSketchRegion(id + "F6", true);
            extrude(context, id + "F7", {"entities" : qUnion([Q0]), "operationType" : NewBodyOperationType.ADD, "depth" : 1 * mm});
        }
    });
